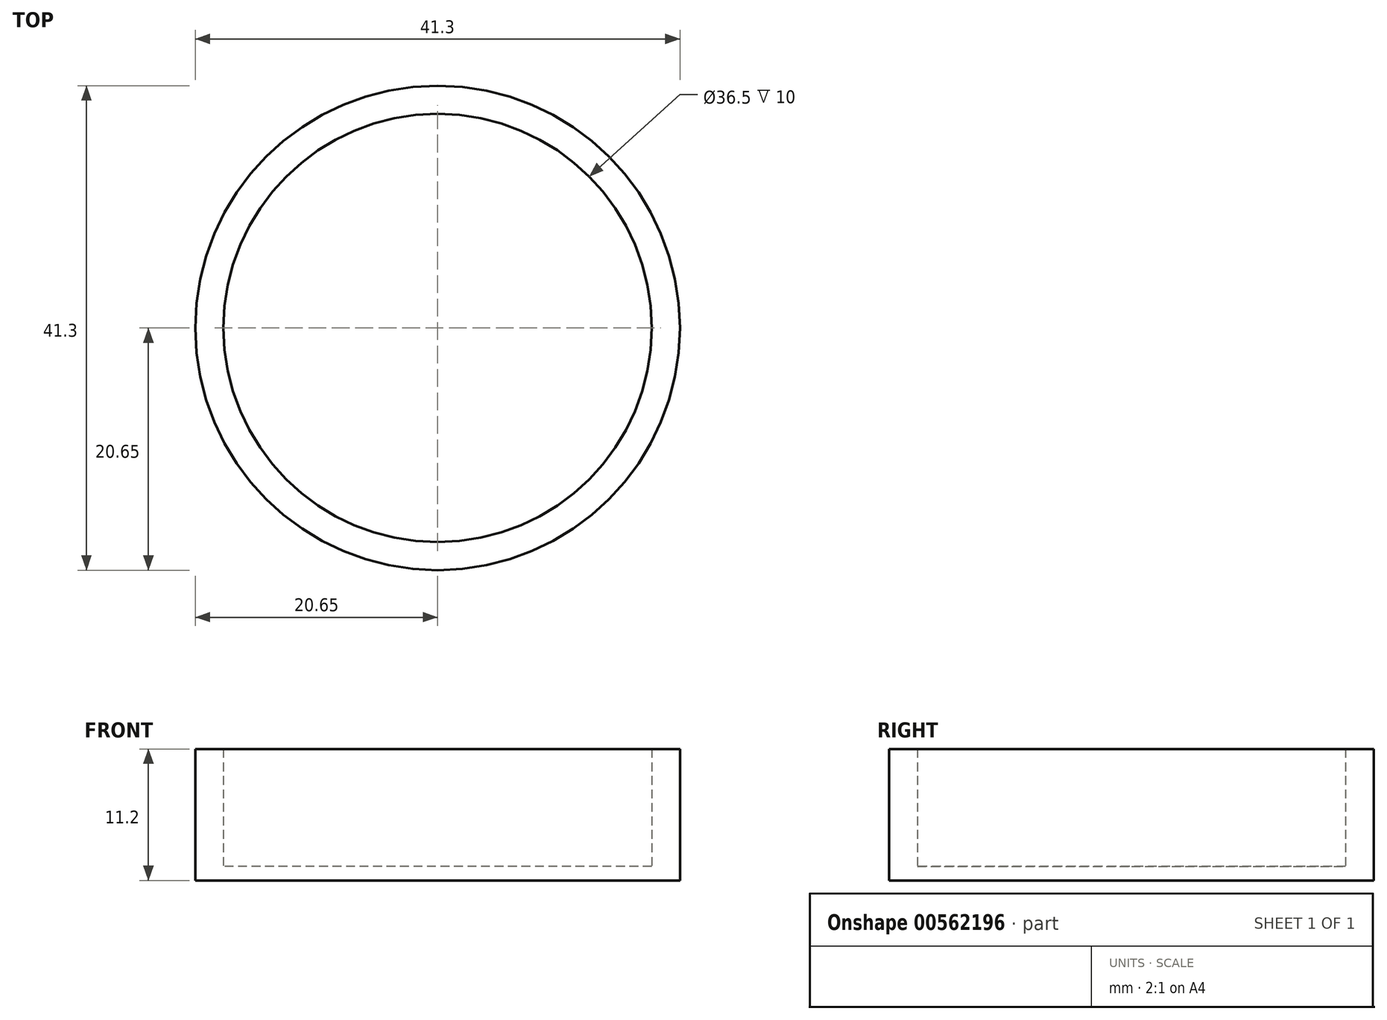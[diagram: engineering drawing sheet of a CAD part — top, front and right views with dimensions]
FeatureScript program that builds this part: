
annotation { "Feature Type Name" : "Feature", "Feature Type Description" : "" }
export const myFeature = defineFeature(function(context is Context, id is Id, definition is map)
    precondition{}
    {
        {
            var Q0;
            Q0=qCreatedBy(makeId("Top.planeOp"),FACE);
            var sketch = newSketch(context, id + "F0", { "sketchPlane" : qUnion([Q0])});
            skCircle(sketch, "E0", {"center": v(0, 0) * mm, "radius": 20.65 * mm});
            skSolve(sketch);
        }
        {
            var Q0;
            Q0=makeQuery(id+"F0.imprint","IMPRINT",FACE,{"disambiguationData":[TD([[makeQuery(id+"F0.imprint","IMPRINT",EDGE,{"derivedFrom":sQuery(id+"F0.wireOp",EDGE,"E0")}),1.0]])]});
            extrude(context, id + "F1", {"entities" : qUnion([Q0]), "depth" : 1.2 * mm, "offsetDistance" : 25 * mm});
        }
        {
            var Q0;
            Q0=makeQuery(id+"F1.opExtrude","CAP_FACE",FACE,{"disambiguationData":[OSD([sQuery(id+"F0.wireOp",EDGE,"E0")])],"isStart":false});
            var sketch = newSketch(context, id + "F2", { "sketchPlane" : qUnion([Q0])});
            skCircle(sketch, "E1.0.0", {"center": v(0, 0) * mm, "radius": 20.65 * mm});
            skCircle(sketch, "E2.0", {"center": v(0, 0) * mm, "radius": 18.25 * mm});
            skSolve(sketch);
        }
        {
            var Q0;
            Q0 = qSketchRegion(id + "F2", true);
            extrude(context, id + "F3", {"entities" : qUnion([Q0]), "operationType" : NewBodyOperationType.ADD, "depth" : 10 * mm, "offsetDistance" : 25 * mm});
        }
    });
